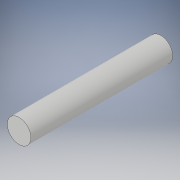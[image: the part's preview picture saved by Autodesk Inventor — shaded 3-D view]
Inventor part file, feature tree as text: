
AUTODESK INVENTOR PART (.ipt)
format: ipt  version: 2018 (Build 220112000, 112)  size: 90,112 bytes
history: native  units: in
note: dims shown in document units (in); Inventor stores cm internally (conversion verified against a paired STEP export)
features: extrude x1, sketch x1
ambient origin geometry x8: Origin, YZ Plane, XZ Plane, XY Plane, X Axis, Y Axis, Z Axis, Center Point
bodies: Solid1 (feature_tree)
feature tree (2):
  extrude  "Extrusion1"  Depth=3.9in TaperAngle=0.0deg
  sketch  "Sketch1"  dims[d0=0.65in d1=3.9in d2=0.0in]
